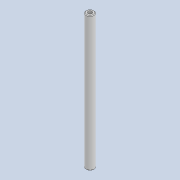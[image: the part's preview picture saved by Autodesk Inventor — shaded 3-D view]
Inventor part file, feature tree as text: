
AUTODESK INVENTOR PART (.ipt)
format: ipt  version: 2020 (Build 240168000, 168)  size: 78,848 bytes
history: native  units: mm
features: extrude x1, chamfer x1, sketch x1
ambient origin geometry x8: Origin, YZ Plane, XZ Plane, XY Plane, X Axis, Y Axis, Z Axis, Center Point
bodies: Solid1 (feature_tree)
feature tree (3):
  extrude  "Extrusion1"  Depth=1.5mm
  chamfer  "Chamfer1"  Distance=50.0mm
  sketch  "Sketch1"  dims[d0=3.0mm d1=1.5mm d2=50.0mm d3=0.0mm d4=0.25mm d5=2.0mm d6=45.0deg]
